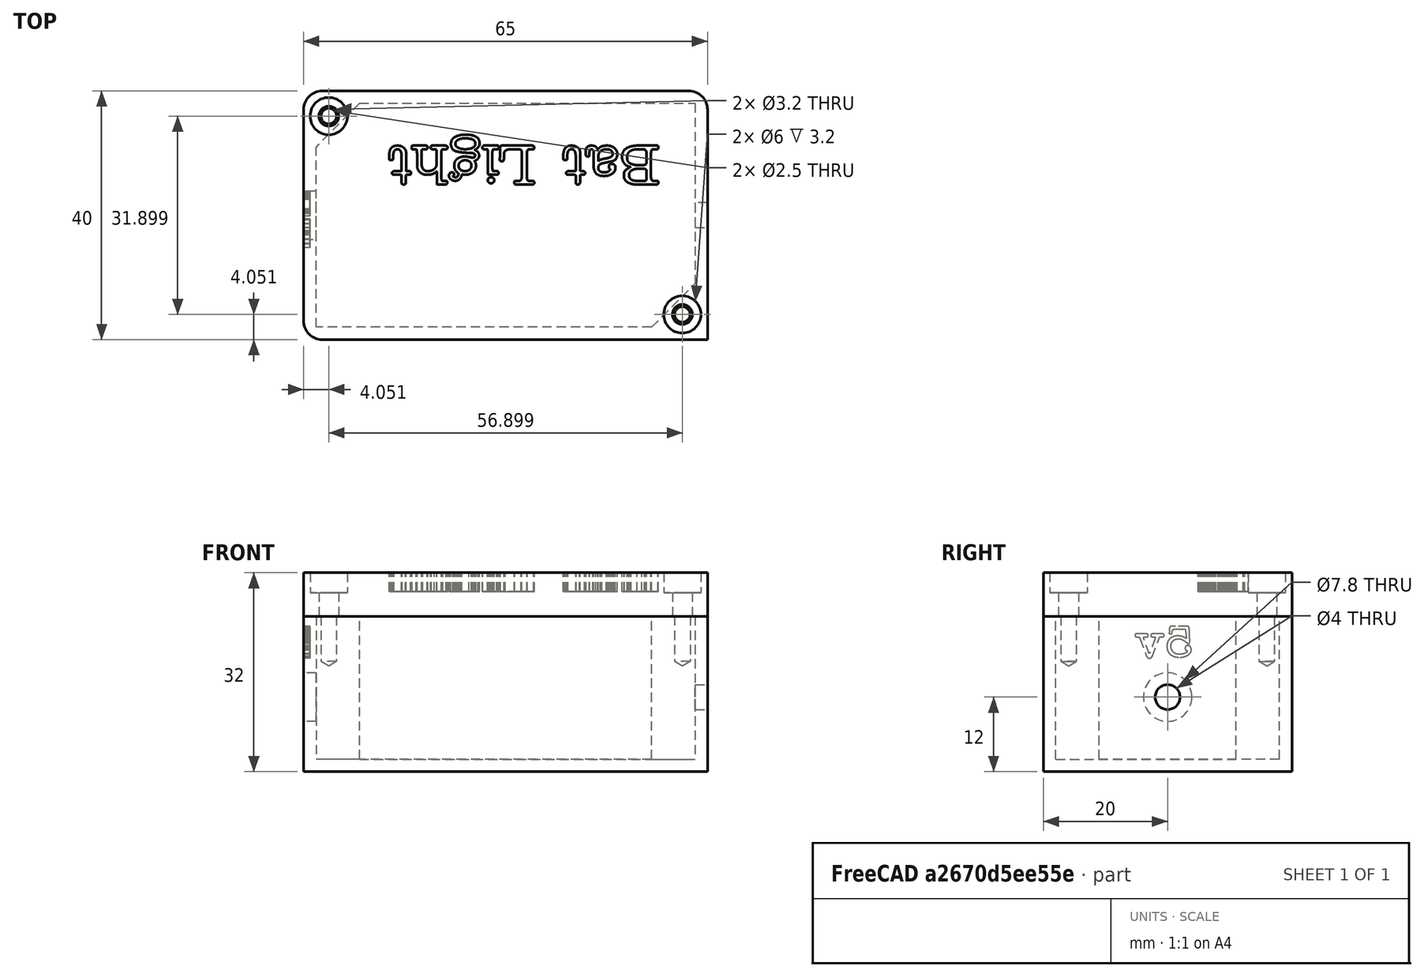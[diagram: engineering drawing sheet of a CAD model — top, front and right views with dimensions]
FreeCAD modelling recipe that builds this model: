
FCSTD DOCUMENT  (FreeCAD 0.18.4R)
Label: box
License: All rights reserved
LicenseURL: http://en.wikipedia.org/wiki/All_rights_reserved
objects: Sketcher::SketchObject×9, PartDesign::Hole×4, Mesh::Feature×3, PartDesign::Pad×3, PartDesign::Pocket×3, PartDesign::ShapeBinder×3, Part::Part2DObjectPython×2, Part::Extrusion×2, PartDesign::Fillet×2, PartDesign::Body×2, Part::Cut×2, PartDesign::Plane×1
note: 43 computed .brp shape members not serialized (recipe doc carries the construction recipe); baked Part::Feature solids carry a one-line shape summary decoded from their .brp

FEATURE [Mesh::Feature] d1_mini  label="d1-mini"
  Placement = pos=(16.4205,20.4343,6.39879) rot=(-0.999429,0.033494,-0.00441;3.13277rad)
FEATURE [Sketcher::SketchObject] Sketch
  MapMode = 5
  Support = -> [XY_Plane]
  sketch-geometry (4):
    g0: LineSegment StartX=0 StartY=40 StartZ=0 EndX=65 EndY=40 EndZ=0
    g1: LineSegment StartX=65 StartY=40 StartZ=0 EndX=65 EndY=0 EndZ=0
    g2: LineSegment StartX=65 StartY=0 StartZ=0 EndX=0 EndY=0 EndZ=0
    g3: LineSegment StartX=0 StartY=0 StartZ=0 EndX=0 EndY=40 EndZ=0
  constraints (11):
    c: Coincident(g0,g1)
    c: Coincident(g1,g2)
    c: Coincident(g2,g3)
    c: Coincident(g3,g0)
    c: Horizontal(g0)
    c: Horizontal(g2)
    c: Vertical(g1)
    c: Vertical(g3)
    c: Coincident(g2,g-1)
    c: DistanceX(g2,g2) = 65
    c: DistanceY(g1,g1) = 40
FEATURE [PartDesign::Pad] Pad
  Length = 25
  Length2 = 100
  Profile = -> Sketch
  Type = 0
FEATURE [Sketcher::SketchObject] Sketch001
  MapMode = 5
  Placement = pos=(0,0,25) rot=(0,0,1;0rad)
  Support = -> [Pad]
  sketch-geometry (4):
    g0: LineSegment StartX=2 StartY=38 StartZ=0 EndX=63 EndY=38 EndZ=0
    g1: LineSegment StartX=63 StartY=38 StartZ=0 EndX=63 EndY=2 EndZ=0
    g2: LineSegment StartX=63 StartY=2 StartZ=0 EndX=2 EndY=2 EndZ=0
    g3: LineSegment StartX=2 StartY=2 StartZ=0 EndX=2 EndY=38 EndZ=0
  constraints (12):
    c: Coincident(g0,g1)
    c: Coincident(g1,g2)
    c: Coincident(g2,g3)
    c: Coincident(g3,g0)
    c: Horizontal(g0)
    c: Horizontal(g2)
    c: Vertical(g1)
    c: Vertical(g3)
    c: DistanceX(g2,g2) = 61
    c: DistanceY(g1,g1) = 36
    c: DistanceX(g2,g-1) = -2
    c: DistanceY(g2,g-1) = -2
FEATURE [PartDesign::Pocket] Pocket
  BaseFeature = -> Pad
  Length = 23
  Length2 = 100
  Profile = -> Sketch001
  Type = 0
FEATURE [Sketcher::SketchObject] Sketch002
  MapMode = 5
  Placement = pos=(0,0,0) rot=(0.57735,-0.57735,-0.57735;2.0944rad)
  Support = -> [Pocket]
  sketch-geometry (1):
    g0: Circle CenterX=-20 CenterY=12 CenterZ=0 NormalX=0 NormalY=0 NormalZ=1 AngleXU=0 Radius=3.9
  constraints (3):
    c: Radius(g0) = 3.9
    c: DistanceX(g0,g-1) = 20
    c: DistanceY(g0,g-1) = -12
FEATURE [Sketcher::SketchObject] Sketch003
  MapMode = 5
  Placement = pos=(65,0,0) rot=(0.57735,0.57735,0.57735;2.0944rad)
  Support = -> [Pocket]
  sketch-geometry (1):
    g0: Circle CenterX=20 CenterY=12 CenterZ=0 NormalX=0 NormalY=0 NormalZ=1 AngleXU=0 Radius=2
  constraints (3):
    c: DistanceX(g0,g-1) = -20
    c: DistanceY(g0,g-1) = -12
    c: Radius(g0) = 2
FEATURE [PartDesign::Pocket] Pocket001
  BaseFeature = -> Pocket
  Length = 5
  Length2 = 100
  Profile = -> Sketch003
  Type = 0
FEATURE [PartDesign::Pocket] Pocket002
  BaseFeature = -> Pocket001
  Length = 5
  Length2 = 100
  Profile = -> Sketch002
  Type = 0
FEATURE [Sketcher::SketchObject] Sketch004
  ExternalGeometry = -> [Pocket002]
  MapMode = 5
  Placement = pos=(0,0,2) rot=(0,0,1;0rad)
  Support = -> [Pocket002]
  sketch-geometry (6):
    g0: LineSegment StartX=2 StartY=38 StartZ=0 EndX=9 EndY=38 EndZ=0
    g1: LineSegment StartX=9 StartY=38 StartZ=0 EndX=2 EndY=31 EndZ=0
    g2: LineSegment StartX=2 StartY=31 StartZ=0 EndX=2 EndY=38 EndZ=0
    g3: LineSegment StartX=63 StartY=9 StartZ=0 EndX=63 EndY=2 EndZ=0
    g4: LineSegment StartX=63 StartY=2 StartZ=0 EndX=56 EndY=2 EndZ=0
    g5: LineSegment StartX=56 StartY=2 StartZ=0 EndX=63 EndY=9 EndZ=0
  constraints (16):
    c: Coincident(g0,g1)
    c: Coincident(g1,g2)
    c: Coincident(g2,g0)
    c: Horizontal(g0)
    c: Vertical(g2)
    c: Coincident(g0,g-4)
    c: DistanceX(g0,g0) = 7
    c: DistanceY(g2,g2) = 7
    c: Coincident(g3,g4)
    c: Coincident(g4,g5)
    c: Coincident(g5,g3)
    c: Vertical(g3)
    c: Horizontal(g4)
    c: DistanceY(g3,g3) = 7
    c: DistanceX(g4,g4) = 7
    c: Coincident(g3,g-6)
FEATURE [PartDesign::Pad] Pad001
  BaseFeature = -> Pocket002
  Length = 23
  Length2 = 100
  Profile = -> Sketch004
  Type = 0
FEATURE [Sketcher::SketchObject] Sketch005
  ExternalGeometry = -> [Pad001]
  MapMode = 5
  Placement = pos=(0,0,25) rot=(0,0,1;0rad)
  Support = -> [Pad001]
  sketch-geometry (2):
    g0: LineSegment [constr] StartX=2 StartY=38 StartZ=0 EndX=5.5 EndY=34.5 EndZ=0
    g1: Circle CenterX=4.05061 CenterY=35.9494 CenterZ=0 NormalX=0 NormalY=0 NormalZ=1 AngleXU=0 Radius=1.6
  constraints (6):
    c: Perpendicular(g0,g-3)
    c: Coincident(g0,g-5)
    c: PointOnObject(g0,g-3)
    c: PointOnObject(g1,g0)
    c: Distance(g1,g0) = 2.9
    c: Radius(g1) = 1.6
FEATURE [PartDesign::Hole] Hole
  BaseFeature = -> Pad001
  Depth = 8
  DepthType = 0
  Diameter = 2.5
  DrillPoint = 1
  DrillPointAngle = 118
  HoleCutCountersinkAngle = 90
  HoleCutDepth = 0
  HoleCutDiameter = 3
  HoleCutType = 0
  ModelActualThread = false
  Profile = -> Sketch005
  Tapered = false
  TaperedAngle = 90
  ThreadAngle = 60
  ThreadClass = 4
  ThreadCutOffInner = 0.0541266
  ThreadCutOffOuter = 0.108253
  ThreadDirection = 1
  ThreadFit = 0
  ThreadPitch = 0.5
  ThreadSize = 3
  ThreadType = 1
  Threaded = true
FEATURE [Sketcher::SketchObject] Sketch006
  ExternalGeometry = -> [Hole]
  MapMode = 5
  Placement = pos=(0,0,25) rot=(0,0,1;0rad)
  Support = -> [Hole]
  sketch-geometry (2):
    g0: LineSegment [constr] StartX=59.5 StartY=5.5 StartZ=0 EndX=63 EndY=2 EndZ=0
    g1: Circle CenterX=60.9494 CenterY=4.05061 CenterZ=0 NormalX=0 NormalY=0 NormalZ=1 AngleXU=0 Radius=1.6
  constraints (6):
    c: Perpendicular(g0,g-3)
    c: Coincident(g0,g-5)
    c: PointOnObject(g0,g-3)
    c: Radius(g1) = 1.6
    c: Distance(g1,g0) = 2.9
    c: PointOnObject(g1,g0)
FEATURE [PartDesign::Hole] Hole001
  BaseFeature = -> Hole
  Depth = 8
  DepthType = 0
  Diameter = 2.5
  DrillPoint = 1
  DrillPointAngle = 118
  HoleCutCountersinkAngle = 90
  HoleCutDepth = 0
  HoleCutDiameter = 3
  HoleCutType = 0
  ModelActualThread = false
  Profile = -> Hole [Face12]
  Tapered = false
  TaperedAngle = 90
  ThreadAngle = 60
  ThreadClass = 4
  ThreadCutOffInner = 0.0541266
  ThreadCutOffOuter = 0.108253
  ThreadDirection = 1
  ThreadFit = 0
  ThreadPitch = 0.5
  ThreadSize = 3
  ThreadType = 1
  Threaded = true
FEATURE [PartDesign::Hole] Hole002
  BaseFeature = -> Hole001
  Depth = 8
  DepthType = 0
  Diameter = 2.5
  DrillPoint = 1
  DrillPointAngle = 118
  HoleCutCountersinkAngle = 90
  HoleCutDepth = 0
  HoleCutDiameter = 3
  HoleCutType = 0
  ModelActualThread = false
  Profile = -> Sketch006
  Tapered = false
  TaperedAngle = 90
  ThreadAngle = 60
  ThreadClass = 4
  ThreadCutOffInner = 0.0541266
  ThreadCutOffOuter = 0.108253
  ThreadDirection = 1
  ThreadFit = 0
  ThreadPitch = 0.5
  ThreadSize = 3
  ThreadType = 1
  Threaded = true
FEATURE [Part::Part2DObjectPython] ShapeString  # Draft 2D object (typed FeaturePython)
  FontFile = <userpath>/Documents/TTF/typewriter/TYPEWR__.TTF
  Placement = pos=(-58.29,62.4,0) rot=(0,0,1;0rad)
  Size = 1.2
  String = 5v
  Tracking = 0
FEATURE [Part::Extrusion] Extrude
  Base = -> ShapeString
  Dir = (0,0,1)
  DirMode = 2
  FaceMakerClass = Part::FaceMakerBullseye
  LengthFwd = 1.2
  LengthRev = 0
  Placement = pos=(1,-34,-44) rot=(-0.57735,0.57735,0.57735;4.18879rad)
  Solid = false
  Symmetric = false
FEATURE [PartDesign::ShapeBinder] CopyCut
  TraceSupport = false
FEATURE [PartDesign::ShapeBinder] CopyCut001
  TraceSupport = false
FEATURE [PartDesign::ShapeBinder] CopyCut002
  TraceSupport = false
FEATURE [PartDesign::Plane] DatumPlane
  Length = 81.1748
  MapMode = 45
  Placement = pos=(32.5,20,25) rot=(0,0,1;1.45602rad)
  ResizeMode = 0
  Support = -> [CopyCut,CopyCut001,CopyCut002]
  Width = 100.648
FEATURE [Sketcher::SketchObject] Sketch007
  ExternalGeometry = -> [CopyCut]
  MapMode = 5
  Placement = pos=(32.5,20,25) rot=(0,0,1;1.45602rad)
  Support = -> [DatumPlane]
  sketch-geometry (4):
    g0: LineSegment StartX=-23.5904 StartY=29.9958 StartZ=0 EndX=16.1465 EndY=34.5766 EndZ=0
    g1: LineSegment StartX=16.1465 StartY=34.5766 StartZ=0 EndX=23.5904 EndY=-29.9958 EndZ=0
    g2: LineSegment StartX=23.5904 StartY=-29.9958 StartZ=0 EndX=-16.1465 EndY=-34.5766 EndZ=0
    g3: LineSegment StartX=-16.1465 StartY=-34.5766 StartZ=0 EndX=-23.5904 EndY=29.9958 EndZ=0
  constraints (8):
    c: Coincident(g0,g1)
    c: Coincident(g1,g2)
    c: Coincident(g2,g3)
    c: Coincident(g3,g0)
    c: Coincident(g0,g-4)
    c: Coincident(g0,g-5)
    c: Coincident(g2,g-6)
    c: Coincident(g1,g-6)
FEATURE [PartDesign::Pad] Pad002
  Length = 7
  Length2 = 100
  Placement = pos=(32.5,20,25) rot=(0,0,1;1.45602rad)
  Profile = -> Sketch007
  Type = 0
FEATURE [Sketcher::SketchObject] Sketch008
  ExternalGeometry = -> [CopyCut001,CopyCut002]
  MapMode = 5
  Placement = pos=(32.5,20,32) rot=(0,0,1;1.45602rad)
  Support = -> [Pad002]
  sketch-geometry (2):
    g0: Circle CenterX=12.5864 CenterY=30.0888 CenterZ=0 NormalX=0 NormalY=0 NormalZ=1 AngleXU=0 Radius=1.6
    g1: Circle CenterX=-12.5864 CenterY=-30.0888 CenterZ=0 NormalX=0 NormalY=0 NormalZ=1 AngleXU=0 Radius=1.6
  constraints (4):
    c: Radius(g1) = 1.6
    c: Equal(g1,g0)
    c: Coincident(g0,g-3)
    c: Coincident(g1,g-4)
FEATURE [PartDesign::Hole] Hole003
  BaseFeature = -> Pad002
  Depth = 25
  DepthType = 0
  Diameter = 3.2
  DrillPoint = 1
  DrillPointAngle = 118
  HoleCutCountersinkAngle = 90
  HoleCutDepth = 3.2
  HoleCutDiameter = 6
  HoleCutType = 1
  ModelActualThread = false
  Placement = pos=(32.5,20,25) rot=(0,0,1;1.45602rad)
  Profile = -> Sketch008
  Tapered = false
  TaperedAngle = 90
  ThreadAngle = 0
  ThreadClass = 0
  ThreadCutOffInner = 0
  ThreadCutOffOuter = 0
  ThreadDirection = 0
  ThreadFit = 0
  ThreadPitch = 0
  ThreadSize = 0
  ThreadType = 0
  Threaded = false
FEATURE [Part::Part2DObjectPython] ShapeString001  # Draft 2D object (typed FeaturePython)
  FontFile = <userpath>/Documents/TTF/typewriter/TYPEWR__.TTF
  Placement = pos=(-16.2766,-21.2109,0) rot=(0,0,1;0rad)
  Size = 1.5
  String = Bat Light
  Tracking = 0
FEATURE [Part::Extrusion] Extrude001
  Base = -> ShapeString001
  Dir = (0,0,1)
  DirMode = 2
  FaceMakerClass = Part::FaceMakerBullseye
  LengthFwd = 3.1
  LengthRev = 0
  Placement = pos=(41,10,29) rot=(0,0,1;3.14159rad)
  Solid = true
  Symmetric = false
FEATURE [PartDesign::Fillet] Fillet
  Base = -> Hole003 [Edge8,Edge2,Edge1]
  BaseFeature = -> Hole003
  Placement = pos=(32.5,20,25) rot=(0,0,1;1.45602rad)
  Radius = 3
FEATURE [PartDesign::Body] Body001  label="capot"
  Group = -> [DatumPlane,CopyCut,CopyCut001,CopyCut002,Sketch007,Pad002,Sketch008,Hole003,Fillet]
  Origin = -> Origin001
  Tip = -> Fillet
FEATURE [Part::Cut] Cut001
  Base = -> Body001
  Tool = -> Extrude001
FEATURE [PartDesign::Fillet] Fillet001
  Base = -> Hole002 [Edge2,Edge1,Edge5]
  BaseFeature = -> Hole002
  Radius = 3
FEATURE [PartDesign::Body] Body
  Group = -> [Sketch,Pad,Sketch001,Pocket,Sketch002,Sketch003,Pocket001,Pocket002,Sketch004,Pad001,Sketch005,Hole,Sketch006,Hole001,Hole002,Fillet001]
  Origin = -> Origin
  Tip = -> Fillet001
FEATURE [Part::Cut] Cut
  Base = -> Body
  Tool = -> Extrude
FEATURE [Mesh::Feature] Mesh  label="Cut001 (Meshed)"
FEATURE [Mesh::Feature] Mesh001  label="Cut (Meshed)"
